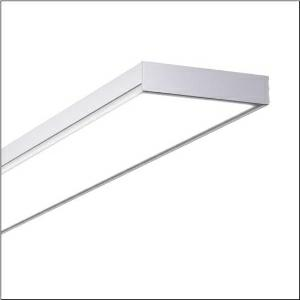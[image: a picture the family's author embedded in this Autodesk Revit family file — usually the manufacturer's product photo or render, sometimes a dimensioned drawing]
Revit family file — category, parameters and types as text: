
# Revit family: apollon_r__31_surface_51mp26wm2341e_8ded
name_source: partatom
category: Lighting Fixtures
units: mm (PartAtom-declared; Revit-internal decimal feet)

## family parameters
Cut with Voids When Loaded = No
Host = Face
Light Source = No
Part Type = Normal
Room Calculation Point = No
Round Connector Dimension = Use Diameter
Shared = No

## types (1)
- Apollon® 31 Surface (1 x LED, 4400 lm, 33 W, 3000K)
    Apparent Load = 33 VA
    CIE Flux Codes = 61 87 97 97 100
    Color Rendering = 80
    Color Temperature = 3000K
    Default Elevation = 1800 mm
    Description = Apollon® 31 Surface, office luminaire, primary optical cover: micro prismatic cover, of PMMA, light emission: direct distribution, primary light characteristic: symmetric, installation type: surface-mounted, LED, rated luminous flux: 4.400lm, luminous efficacy: 133lm/W, light colour: 830, colour temperature: 3000K, control gear: ON/OFF Multilumen, with terminal, 3-pole, mains connection: 220..240V, AC, 50/60Hz, rated input power: 33W, housing, of sheet steel, coil coated, metallic grey (RAL 9006), length: 1.545mm, width: 200mm, height: 44mm, protection rating (complete): IP20, insulation class (complete): insulation class II (safety insulation), certification: CE, impact resistance: IK02, permissible operating ambient temperature: -20..+40°C, packaging unit: 1 piece
    Height = 44 mm
    Lamp = 1 x LED
    Lamp Light Flux = 4400 lm
    Lamp Power = 33 W
    Lamp count = 1
    Length = 1545 mm
    Luminous efficacy = 133 lm/W
    Manufacturer = Siteco
    ModVariant = No
    Model = 51MP26WM2341E
    Mounting Place = Ceiling
    Mounting Type = Surface mounted
    Number of Poles = 1
    OnlyDefault = Yes
    Power Factor = 1
    Product Name = Apollon® 31 Surface
    Product group = office luminaire | ceiling mounted
    ProductGroupID = 303
    Protection Class = Protection class II
    Protection Degree = IP 20
    RLX_Detail_Level = 1
    RLX_Emergency_Light_Flux = 0 lm
    RLX_Emergency_Type = 0
    RLX_Emergency_Type_DB = No
    RlxData = <blob elided: 24101 chars, md5=3ad49e6a>
    Socket = socket
    Standby Power = 0 W
    System Light Flux = 4400 lm
    System Power = 33 W
    Type Comments = Product without accessories
    Type Image = l_1313654.jpg
    URL = http://relux.com
    VarID = ---
    Voltage = 0 V
    Weight = 0.00 kg
    Width = 200 mm  [stored 0.656168 ft]

note: [stored X ft] marks values corroborated as IEEE doubles in the binary element streams (Revit-internal decimal feet)

## geometry (parser evidence)
native form markers: Blend x4, Sweep x11
no freeform markers — native parametric forms only
